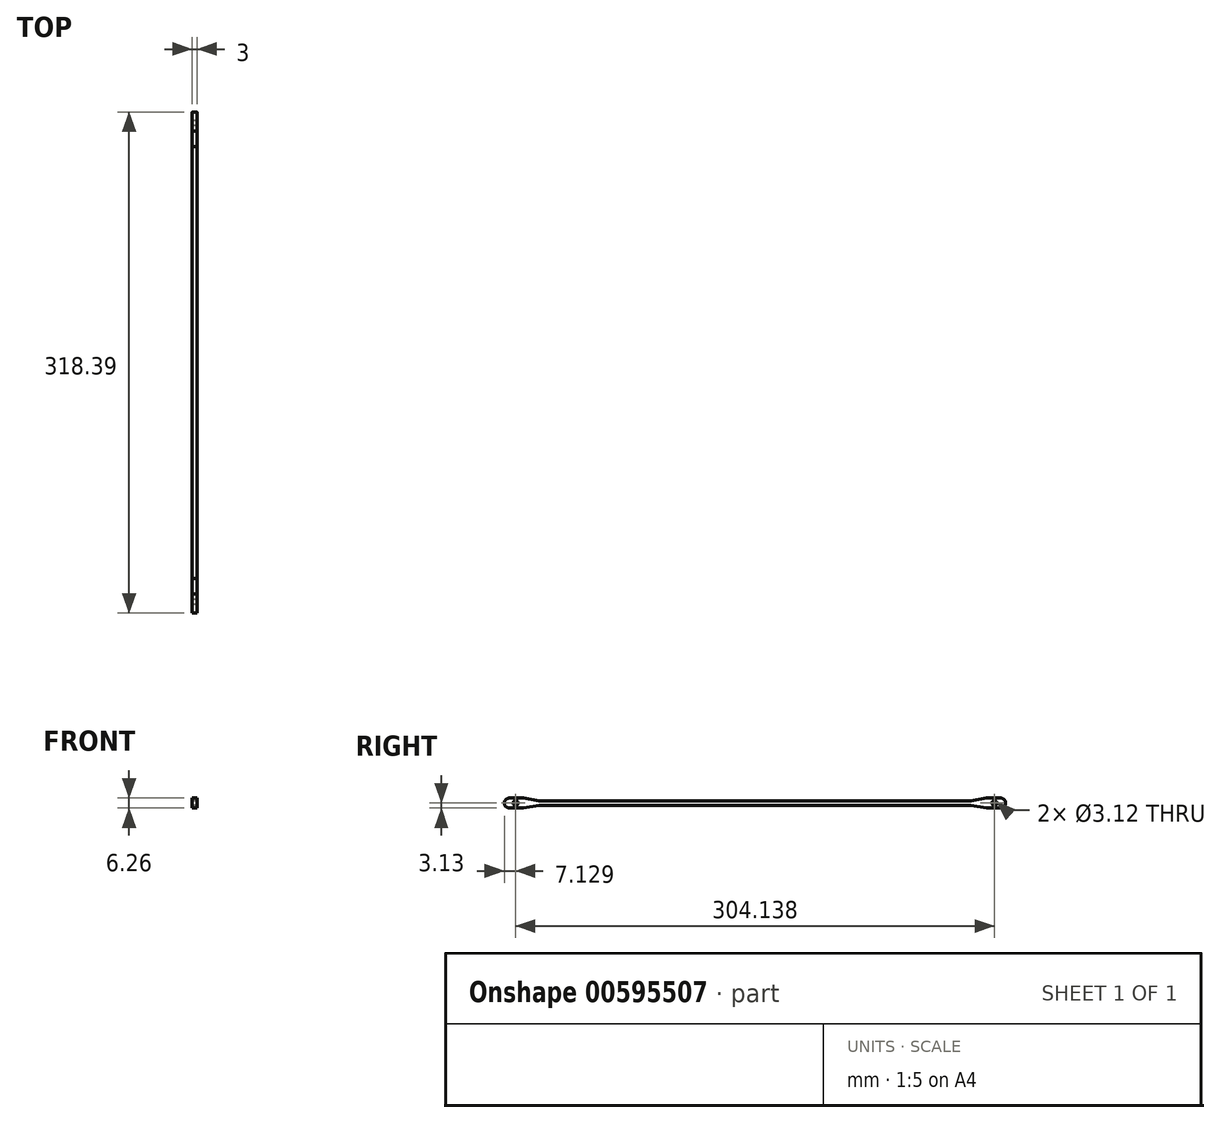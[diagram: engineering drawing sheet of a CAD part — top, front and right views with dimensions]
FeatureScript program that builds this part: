
annotation { "Feature Type Name" : "Feature", "Feature Type Description" : "" }
export const myFeature = defineFeature(function(context is Context, id is Id, definition is map)
    precondition{}
    {
        {
            var Q0;
            Q0=qCreatedBy(makeId("Right.planeOp"),FACE);
            var sketch = newSketch(context, id + "F0", { "sketchPlane" : qUnion([Q0])});
            skCircle(sketch, "E0", {"center": v(206.26, 1.5) * mm, "radius": 1.56 * mm});
            skLineSegment(sketch, "E1.bottom", {"start": v(201.26, 4.63) * mm, "end": v(210.26, 4.63) * mm});
            skLineSegment(sketch, "E1.top", {"start": v(201.26, -1.63) * mm, "end": v(210.26, -1.63) * mm});
            skArc(sketch, "E2", {"start": v(210.26, -1.63) * mm, "mid": v(213.38, 1.5) * mm, "end": v(210.26, 4.62) * mm});
            skLineSegment(sketch, "E3", {"start": v(201.26, 4.63) * mm, "end": v(191.26, 3) * mm});
            skLineSegment(sketch, "E4", {"start": v(201.26, -1.63) * mm, "end": v(191.26, 0) * mm});
            skCircle(sketch, "E5.MirrorC", {"center": v(-97.88, 1.5) * mm, "radius": 1.56 * mm});
            skLineSegment(sketch, "E6.MirrorCS", {"start": v(-92.88, 4.62) * mm, "end": v(-101.88, 4.62) * mm});
            skLineSegment(sketch, "E7.MirrorCS", {"start": v(-92.88, -1.63) * mm, "end": v(-101.88, -1.63) * mm});
            skLineSegment(sketch, "E8.MirrorCS", {"start": v(-92.88, 4.62) * mm, "end": v(-82.88, 3) * mm});
            skArc(sketch, "E9.MirrorCS", {"start": v(-101.88, -1.63) * mm, "mid": v(-105, 1.5) * mm, "end": v(-101.88, 4.62) * mm});
            skLineSegment(sketch, "E10.MirrorCS", {"start": v(-92.88, -1.63) * mm, "end": v(-82.88, 0) * mm});
            skLineSegment(sketch, "E11", {"start": v(-82.88, 3) * mm, "end": v(191.26, 3) * mm});
            skLineSegment(sketch, "E12", {"start": v(191.26, 0) * mm, "end": v(-82.88, 0) * mm});
            skSolve(sketch);
        }
        {
            var Q0;
            Q0 = qSketchRegion(id + "F0", true);
            extrude(context, id + "F1", {"entities" : qUnion([Q0]), "depth" : 3 * mm, "offsetDistance" : 25 * mm});
        }
    });
